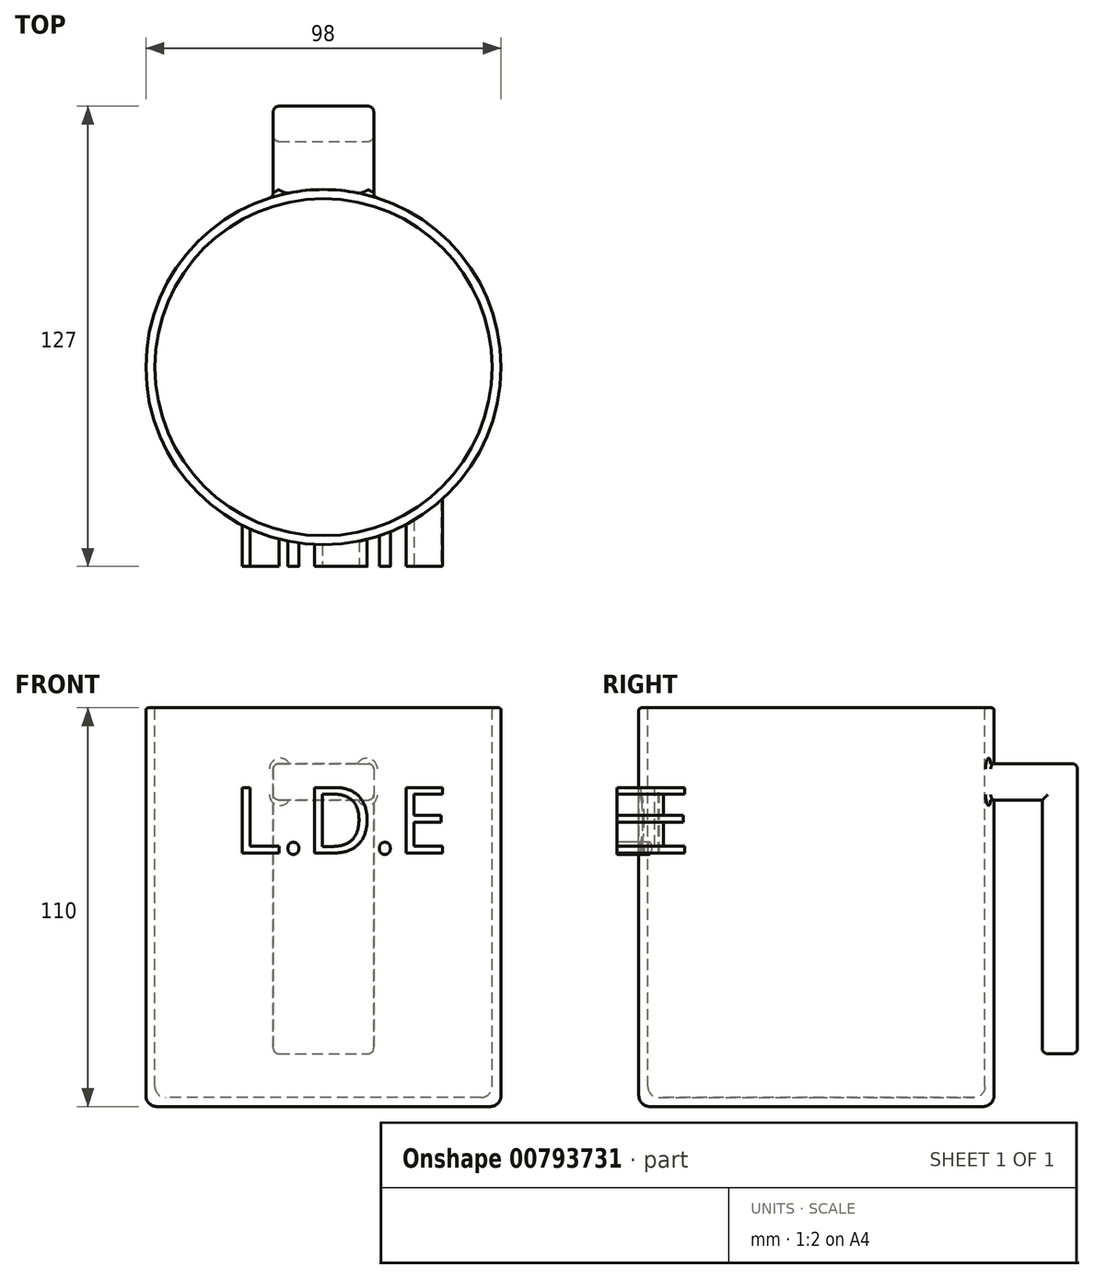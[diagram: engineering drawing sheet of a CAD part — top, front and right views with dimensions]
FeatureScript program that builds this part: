
annotation { "Feature Type Name" : "Feature", "Feature Type Description" : "" }
export const myFeature = defineFeature(function(context is Context, id is Id, definition is map)
    precondition{}
    {
        {
            var Q0;
            Q0=qCreatedBy(makeId("Top.planeOp"),FACE);
            cPlane(context, id + "F0", {"entities" : qUnion([Q0]), "cplaneType" : CPlaneType.OFFSET, "offset" : 45 * mm, "width" : 150 * mm, "height" : 150 * mm});
        }
        {
            var Q0;
            Q0=qCreatedBy(id+"F0.planeOp",FACE);
            var sketch = newSketch(context, id + "F1", { "sketchPlane" : qUnion([Q0])});
            skCircle(sketch, "E0", {"center": v(0, 0) * mm, "radius": 49 * mm});
            skSolve(sketch);
        }
        {
            var Q0;
            Q0=makeQuery(id+"F1.imprint","IMPRINT",FACE,{"disambiguationData":[TD([[makeQuery(id+"F1.imprint","IMPRINT",EDGE,{"derivedFrom":sQuery(id+"F1.wireOp",EDGE,"E0")}),1.0]])]});
            extrude(context, id + "F2", {"entities" : qUnion([Q0]), "oppositeDirection" : true, "depth" : 110 * mm, "offsetDistance" : 25 * mm});
        }
        {
            var Q0;
            Q0=makeQuery(id+"F2.opExtrude","CAP_FACE",FACE,{"disambiguationData":[OSD([sQuery(id+"F1.wireOp",EDGE,"E0")])],"isStart":true});
            shell(context, id + "F3", {"entities" : qUnion([Q0]), "thickness" : 2.5 * mm});
        }
        {
            var Q0;
            Q0=qCreatedBy(makeId("Front.planeOp"),FACE);
            cPlane(context, id + "F4", {"entities" : qUnion([Q0]), "cplaneType" : CPlaneType.OFFSET, "offset" : 72 * mm, "oppositeDirection" : true, "width" : 150 * mm, "height" : 150 * mm});
        }
        {
            var Q0;
            Q0=qCreatedBy(id+"F4.planeOp",FACE);
            var sketch = newSketch(context, id + "F5", { "sketchPlane" : qUnion([Q0])});
            skLineSegment(sketch, "E1.bottom", {"start": v(0, 29.6) * mm, "end": v(-13.86, 29.6) * mm});
            skLineSegment(sketch, "E1.top", {"start": v(0, 19.57) * mm, "end": v(-13.86, 19.57) * mm});
            skLineSegment(sketch, "E1.left", {"start": v(0, 29.6) * mm, "end": v(0, 19.57) * mm});
            skLineSegment(sketch, "E1.right", {"start": v(-13.86, 29.6) * mm, "end": v(-13.86, 19.57) * mm});
            skLineSegment(sketch, "E2.MirrorCS", {"start": v(0, 29.6) * mm, "end": v(13.86, 29.6) * mm});
            skLineSegment(sketch, "E3.MirrorCS", {"start": v(13.86, 29.6) * mm, "end": v(13.86, 19.57) * mm});
            skLineSegment(sketch, "E4.MirrorCS", {"start": v(0, 19.57) * mm, "end": v(13.86, 19.57) * mm});
            skSolve(sketch);
        }
        {
            var Q0;
            Q0=makeQuery(id+"F5.imprint","IMPRINT",FACE,{"disambiguationData":[TD([[makeQuery(id+"F5.imprint","IMPRINT",EDGE,{"derivedFrom":sQuery(id+"F5.wireOp",EDGE,"E1.left")}),1.0]])]});
            var Q1;
            Q1=makeQuery(id+"F5.imprint","IMPRINT",FACE,{"disambiguationData":[TD([[makeQuery(id+"F5.imprint","IMPRINT",EDGE,{"derivedFrom":sQuery(id+"F5.wireOp",EDGE,"E1.bottom")}),1.0]])]});
            extrude(context, id + "F6", {"entities" : qUnion([Q0, Q1]), "operationType" : NewBodyOperationType.ADD, "endBound" : BoundingType.UP_TO_NEXT, "depth" : 25 * mm, "offsetDistance" : 25 * mm});
        }
        {
            var Q0;
            Q0=makeQuery(id+"F6.opExtrude","SWEPT_FACE",FACE,{"disambiguationData":[OSD([sQuery(id+"F5.wireOp",EDGE,"E1.top"),sQuery(id+"F5.wireOp",EDGE,"E4.MirrorCS")])]});
            var sketch = newSketch(context, id + "F7", { "sketchPlane" : qUnion([Q0])});
            skLineSegment(sketch, "E5.bottom", {"start": v(-13.86, -62.32) * mm, "end": v(13.86, -62.32) * mm});
            skLineSegment(sketch, "E5.top", {"start": v(-13.86, -72) * mm, "end": v(13.86, -72) * mm});
            skLineSegment(sketch, "E5.left", {"start": v(-13.86, -62.32) * mm, "end": v(-13.86, -72) * mm});
            skLineSegment(sketch, "E5.right", {"start": v(13.86, -62.32) * mm, "end": v(13.86, -72) * mm});
            skSolve(sketch);
        }
        {
            var Q0;
            Q0=makeQuery(id+"F7.imprint","IMPRINT",FACE,{"disambiguationData":[TD([[makeQuery(id+"F7.imprint","IMPRINT",EDGE,{"derivedFrom":sQuery(id+"F7.wireOp",EDGE,"E5.bottom")}),-1.0]])]});
            extrude(context, id + "F8", {"entities" : qUnion([Q0]), "operationType" : NewBodyOperationType.ADD, "depth" : 70 * mm, "offsetDistance" : 25 * mm});
        }
        {
            var Q0;
            {var subQ0=sQuery(id+"F1.wireOp",EDGE,"E0");Q0=makeQuery(id+"F3.opShell","OFFSET_EDGE",EDGE,{"disambiguationData":[OSD([subQ0]),TDD([makeQuery(id+"F2.opExtrude","CAP_EDGE",EDGE,{"disambiguationData":[OSD([subQ0])],"isStart":true})])]});}
            var Q1;
            Q1=makeQuery(id+"F2.opExtrude","CAP_FACE",FACE,{"disambiguationData":[OSD([sQuery(id+"F1.wireOp",EDGE,"E0")])],"isStart":true});
            fillet(context, id + "F9", {"entities" : qUnion([Q0, Q1]), "radius" : 0.7 * mm, "tangentPropagation" : true, "allowEdgeOverflow" : false});
        }
        {
            var Q0;
            Q0=makeQuery(id+"F8.boolean.opBoolean","MERGE",FACE,{"derivedFrom":[makeQuery(id+"F6.opExtrude","SWEPT_FACE",FACE,{"disambiguationData":[OSD([sQuery(id+"F5.wireOp",EDGE,"E1.right")])]}),makeQuery(id+"F8.opExtrude","SWEPT_FACE",FACE,{"disambiguationData":[OSD([sQuery(id+"F7.wireOp",EDGE,"E5.left")])]})]});
            var Q1;
            Q1=makeQuery(id+"F8.boolean.opBoolean","MERGE",FACE,{"derivedFrom":[makeQuery(id+"F6.opExtrude","SWEPT_FACE",FACE,{"disambiguationData":[OSD([sQuery(id+"F5.wireOp",EDGE,"E3.MirrorCS")])]}),makeQuery(id+"F8.opExtrude","SWEPT_FACE",FACE,{"disambiguationData":[OSD([sQuery(id+"F7.wireOp",EDGE,"E5.right")])]})]});
            var Q2;
            Q2=makeQuery(id+"F6.opExtrude","CAP_EDGE",EDGE,{"disambiguationData":[OSD([sQuery(id+"F5.wireOp",EDGE,"E1.bottom"),sQuery(id+"F5.wireOp",EDGE,"E2.MirrorCS")])],"isStart":true});
            var Q3;
            Q3=makeQuery(id+"F8.opExtrude","CAP_FACE",FACE,{"disambiguationData":[OSD([sQuery(id+"F7.wireOp",EDGE,"E5.bottom"),sQuery(id+"F7.wireOp",EDGE,"E5.top"),sQuery(id+"F7.wireOp",EDGE,"E5.left"),sQuery(id+"F7.wireOp",EDGE,"E5.right")])],"isStart":false});
            var Q4;
            Q4=makeQuery(id+"F8.opExtrude","CAP_EDGE",EDGE,{"disambiguationData":[OSD([sQuery(id+"F7.wireOp",EDGE,"E5.bottom")])],"isStart":true});
            fillet(context, id + "F10", {"entities" : qUnion([Q0, Q1, Q2, Q3, Q4]), "radius" : 1.5 * mm, "tangentPropagation" : true, "allowEdgeOverflow" : false});
        }
        {
            var Q0;
            Q0=qCreatedBy(makeId("Front.planeOp"),FACE);
            cPlane(context, id + "F11", {"entities" : qUnion([Q0]), "cplaneType" : CPlaneType.OFFSET, "offset" : 55 * mm, "width" : 150 * mm, "height" : 150 * mm});
        }
        {
            var Q0;
            Q0=qCreatedBy(id+"F11.planeOp",FACE);
            var sketch = newSketch(context, id + "F12", { "sketchPlane" : qUnion([Q0])});
            skText(sketch, "E6", { "text": "L.D.E", "fontName": "OpenSans-Regular.ttf"});
            const initialGuessF12  = {"E6": [-0.02483, 0.00492, 1, 0, 0.01826]};
            skSetInitialGuess(sketch, initialGuessF12);
            skSolve(sketch);
        }
        {
            var Q0;
            Q0 = qSketchRegion(id + "F12", true);
            extrude(context, id + "F13", {"entities" : qUnion([Q0]), "endBound" : BoundingType.UP_TO_NEXT, "oppositeDirection" : true, "depth" : 25 * mm, "offsetDistance" : 25 * mm});
        }
        {
            var Q0;
            {var subQ0=sQuery(id+"F1.wireOp",EDGE,"E0");Q0=makeQuery(id+"F3.opShell","OFFSET_FACE",FACE,{"disambiguationData":[OSD([subQ0]),TDD([makeQuery(id+"F2.opExtrude","SWEPT_FACE",FACE,{"disambiguationData":[OSD([subQ0])]})])]});}
            fillet(context, id + "F14", {"entities" : qUnion([Q0]), "radius" : 3 * mm, "tangentPropagation" : true, "allowEdgeOverflow" : false});
        }
        {
            var Q0;
            Q0=makeQuery(id+"F2.opExtrude","CAP_FACE",FACE,{"disambiguationData":[OSD([sQuery(id+"F1.wireOp",EDGE,"E0")])],"isStart":false});
            fillet(context, id + "F15", {"entities" : qUnion([Q0]), "radius" : 3 * mm, "tangentPropagation" : true, "allowEdgeOverflow" : false});
        }
    });
